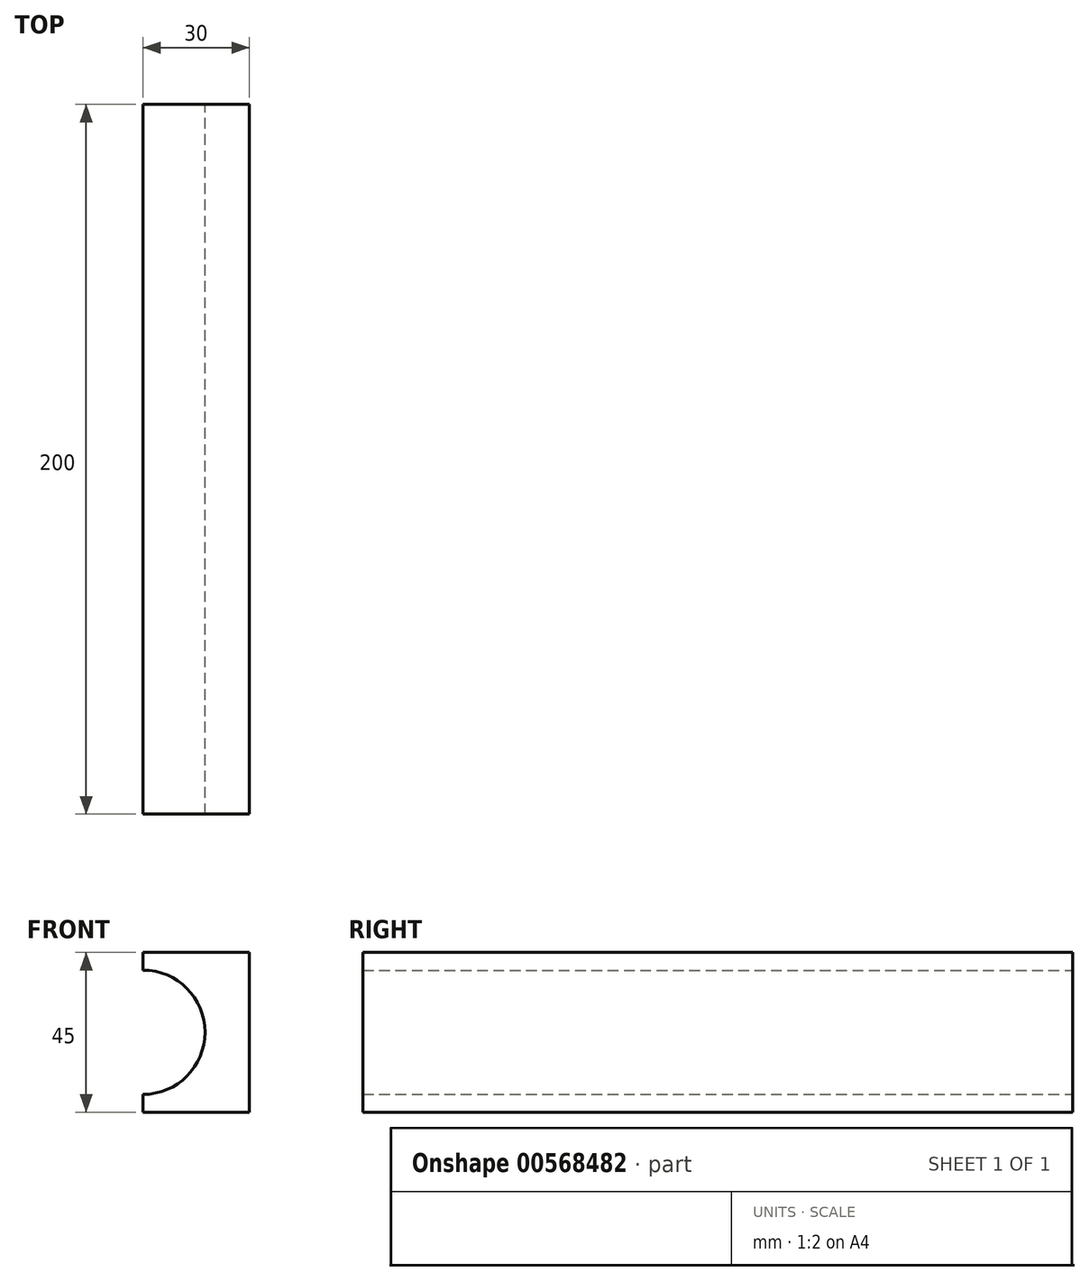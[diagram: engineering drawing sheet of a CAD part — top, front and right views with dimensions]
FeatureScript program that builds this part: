
annotation { "Feature Type Name" : "Feature", "Feature Type Description" : "" }
export const myFeature = defineFeature(function(context is Context, id is Id, definition is map)
    precondition{}
    {
        {
            var Q0;
            Q0=qCreatedBy(makeId("Front.planeOp"),FACE);
            var sketch = newSketch(context, id + "F0", { "sketchPlane" : qUnion([Q0])});
            skLineSegment(sketch, "E0.bottom", {"start": v(-15, -22.5) * mm, "end": v(15, -22.5) * mm});
            skLineSegment(sketch, "E0.top", {"start": v(-15, 22.5) * mm, "end": v(15, 22.5) * mm});
            skLineSegment(sketch, "E0.left", {"start": v(-15, -22.5) * mm, "end": v(-15, -17.5) * mm});
            skLineSegment(sketch, "E0.right", {"start": v(15, -22.5) * mm, "end": v(15, 22.5) * mm});
            skLineSegment(sketch, "E1", {"start": v(0, 72.1) * mm, "end": v(0, -70.45) * mm, "construction": true});
            skLineSegment(sketch, "E2", {"start": v(-60.96, 0) * mm, "end": v(57.64, 0) * mm, "construction": true});
            skArc(sketch, "E3", {"start": v(-15, -17.5) * mm, "mid": v(2.5, 0) * mm, "end": v(-15, 17.5) * mm});
            skLineSegment(sketch, "E4.trimOffspring", {"start": v(-15, 17.5) * mm, "end": v(-15, 22.5) * mm});
            skSolve(sketch);
        }
        {
            var Q0;
            {var subQ0=sQuery(id+"F0.wireOp",EDGE,"E4.trimOffspring");Q0=makeQuery(id+"F0.imprint","IMPRINT",FACE,{"disambiguationData":[TD([[makeQuery(id+"F0.imprint","IMPRINT",EDGE,{"derivedFrom":subQ0}),-1.0]])]});}
            var Q1;
            {var subQ1=sQuery(id+"F0.wireOp",EDGE,"E0.right");var subQ6=sQuery(id+"F0.wireOp",EDGE,"E0.top");var subQ9=makeQuery(id+"F0.imprint","INTERSECT",VERTEX,{"derivedFrom":[subQ6,subQ1]});Q1=makeQuery(id+"F0.imprint","IMPRINT",FACE,{"disambiguationData":[TD([[makeQuery(id+"F0.imprint","IMPRINT",EDGE,{"disambiguationData":[TD([[subQ9,1.0]])],"derivedFrom":subQ6}),-1.0]])]});}
            var Q2;
            {var subQ1=sQuery(id+"F0.wireOp",EDGE,"E0.right");var subQ5=sQuery(id+"F0.wireOp",EDGE,"E0.bottom");var subQ6=makeQuery(id+"F0.imprint","INTERSECT",VERTEX,{"derivedFrom":[subQ5,subQ1]});Q2=makeQuery(id+"F0.imprint","IMPRINT",FACE,{"disambiguationData":[TD([[makeQuery(id+"F0.imprint","IMPRINT",EDGE,{"disambiguationData":[TD([[subQ6,1.0]])],"derivedFrom":subQ5}),1.0]])]});}
            var Q3;
            {var subQ0=sQuery(id+"F0.wireOp",EDGE,"E0.left");Q3=makeQuery(id+"F0.imprint","IMPRINT",FACE,{"disambiguationData":[TD([[makeQuery(id+"F0.imprint","IMPRINT",EDGE,{"derivedFrom":subQ0}),-1.0]])]});}
            extrude(context, id + "F1", {"entities" : qUnion([Q0, Q1, Q2, Q3]), "endBound" : BoundingType.SYMMETRIC, "depth" : 200 * mm, "offsetDistance" : 25 * mm});
        }
    });
